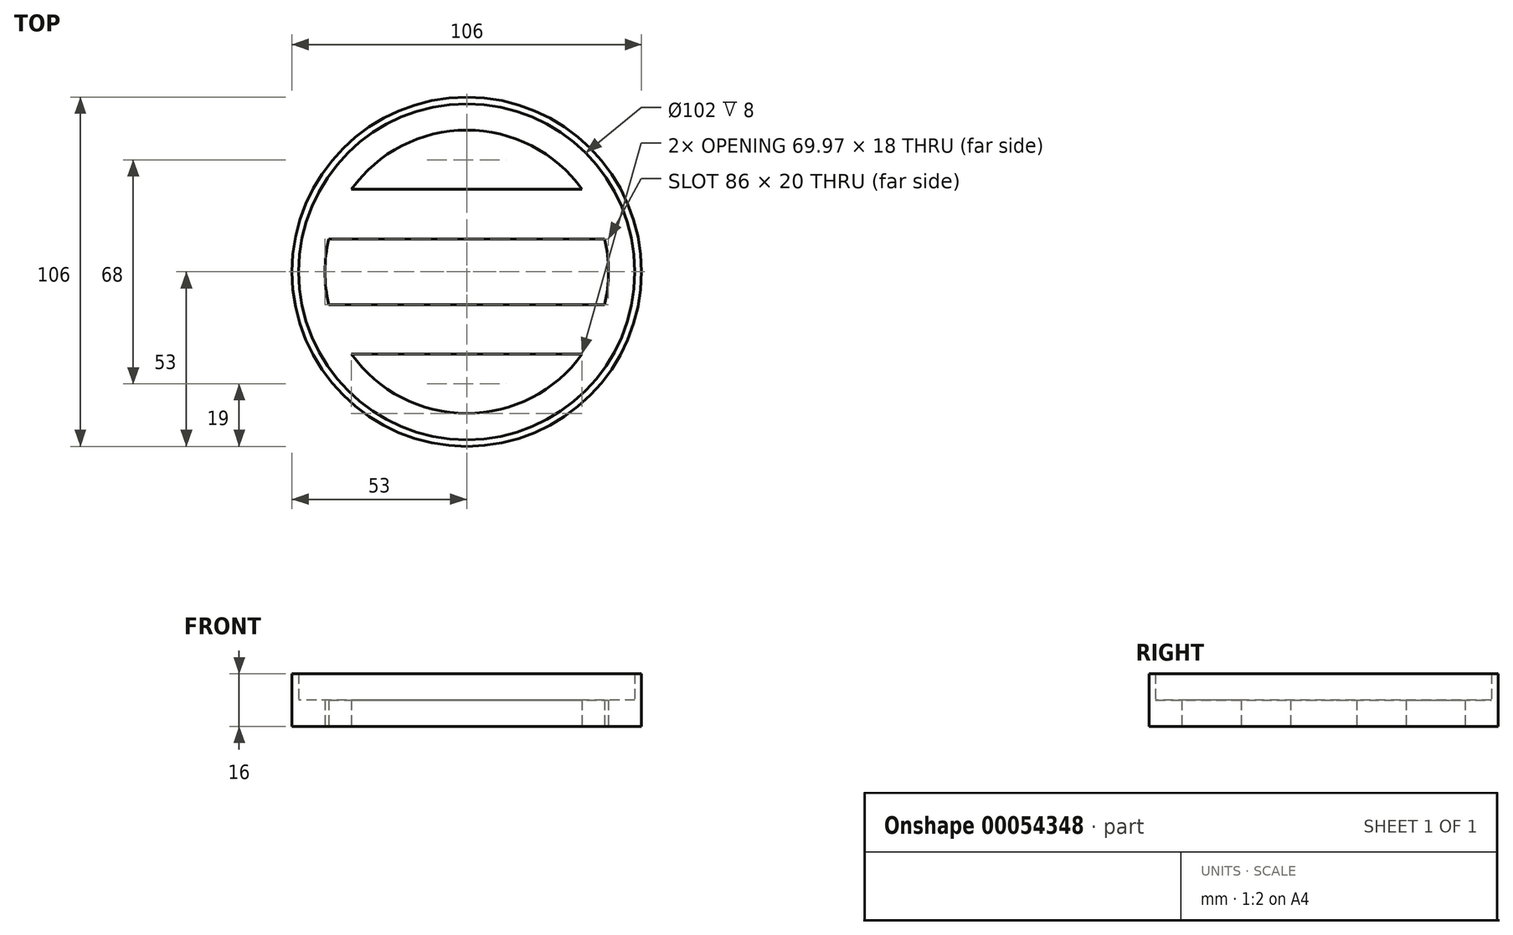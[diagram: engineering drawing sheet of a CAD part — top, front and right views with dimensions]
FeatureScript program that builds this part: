
annotation { "Feature Type Name" : "Feature", "Feature Type Description" : "" }
export const myFeature = defineFeature(function(context is Context, id is Id, definition is map)
    precondition{}
    {
        {
            var Q0;
            Q0=qCreatedBy(makeId("Top.planeOp"),FACE);
            var sketch = newSketch(context, id + "F0", { "sketchPlane" : qUnion([Q0])});
            skCircle(sketch, "E0", {"center": v(0, 0) * mm, "radius": 51 * mm});
            skCircle(sketch, "E1", {"center": v(0, 0) * mm, "radius": 43 * mm});
            skCircle(sketch, "E2", {"center": v(0, 0) * mm, "radius": 53 * mm});
            skLineSegment(sketch, "E3", {"start": v(-41.82, 10) * mm, "end": v(41.82, 10) * mm});
            skLineSegment(sketch, "E4", {"start": v(-41.82, -10) * mm, "end": v(41.82, -10) * mm});
            skLineSegment(sketch, "E5", {"start": v(-34.99, 25) * mm, "end": v(34.99, 25) * mm});
            skLineSegment(sketch, "E6", {"start": v(-34.99, -25) * mm, "end": v(34.99, -25) * mm});
            skSolve(sketch);
        }
        {
            var Q0;
            Q0=makeQuery(id+"F0.imprint","IMPRINT",FACE,{"disambiguationData":[TD([[makeQuery(id+"F0.imprint","IMPRINT",EDGE,{"derivedFrom":sQuery(id+"F0.wireOp",EDGE,"E0")}),1.0]])]});
            var Q1;
            {var subQ0=sQuery(id+"F0.wireOp",EDGE,"E3");Q1=makeQuery(id+"F0.imprint","IMPRINT",FACE,{"disambiguationData":[TD([[makeQuery(id+"F0.imprint","IMPRINT",EDGE,{"derivedFrom":subQ0}),1.0]])]});}
            var Q2;
            {var subQ0=sQuery(id+"F0.wireOp",EDGE,"E4");Q2=makeQuery(id+"F0.imprint","IMPRINT",FACE,{"disambiguationData":[TD([[makeQuery(id+"F0.imprint","IMPRINT",EDGE,{"derivedFrom":subQ0}),-1.0]])]});}
            extrude(context, id + "F1", {"entities" : qUnion([Q0, Q1, Q2]), "depth" : 8 * mm});
        }
        {
            var Q0;
            Q0=makeQuery(id+"F0.imprint","IMPRINT",FACE,{"disambiguationData":[TD([[makeQuery(id+"F0.imprint","IMPRINT",EDGE,{"derivedFrom":sQuery(id+"F0.wireOp",EDGE,"E0")}),-1.0]])]});
            extrude(context, id + "F2", {"entities" : qUnion([Q0]), "operationType" : NewBodyOperationType.ADD, "depth" : 16 * mm});
        }
    });
